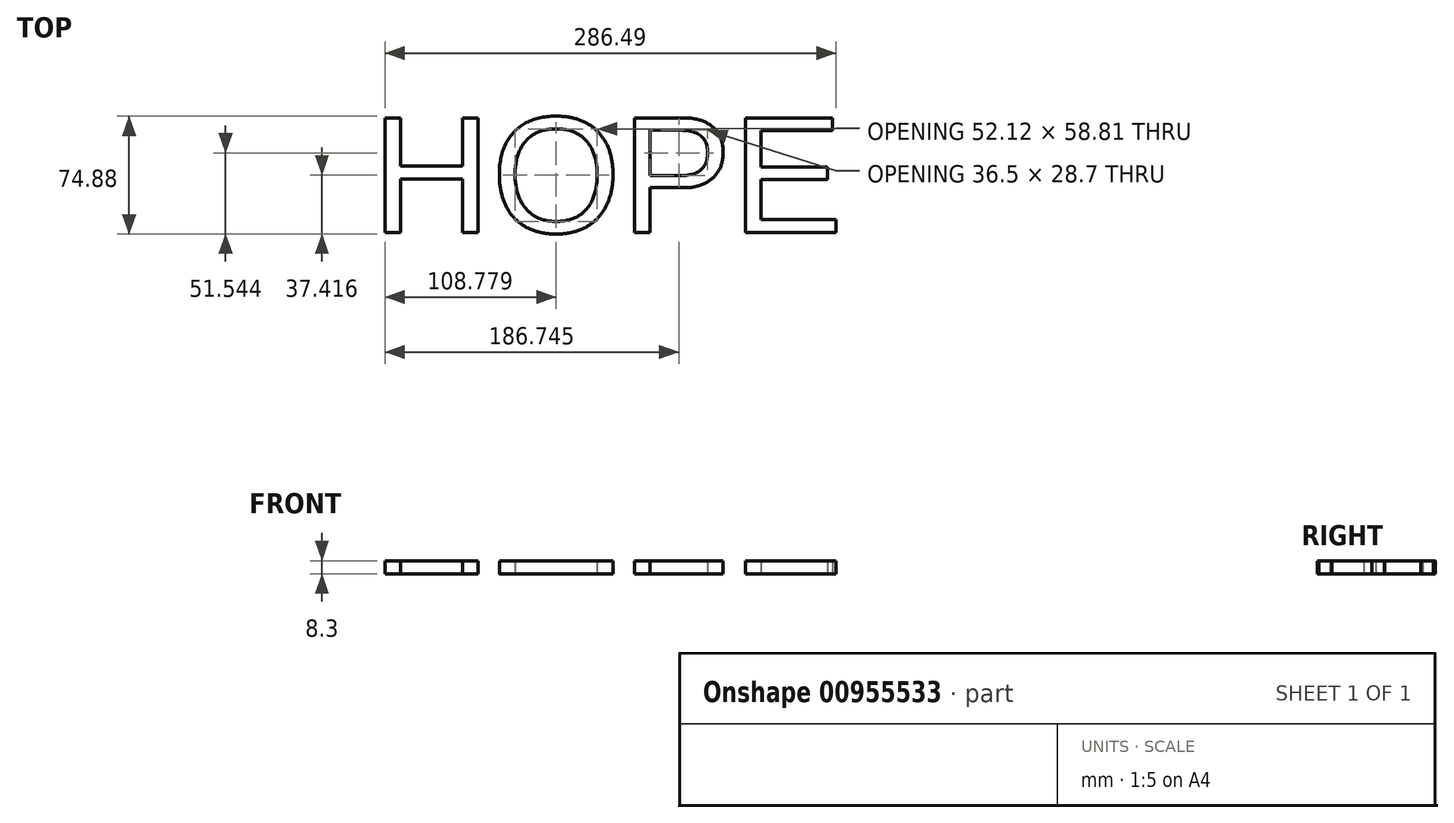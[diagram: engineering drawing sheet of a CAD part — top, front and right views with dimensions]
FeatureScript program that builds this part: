
annotation { "Feature Type Name" : "Feature", "Feature Type Description" : "" }
export const myFeature = defineFeature(function(context is Context, id is Id, definition is map)
    precondition{}
    {
        {
            var Q0;
            Q0=qCreatedBy(makeId("Top.planeOp"),FACE);
            var sketch = newSketch(context, id + "F0", { "sketchPlane" : qUnion([Q0])});
            skText(sketch, "E0", { "text": "HOPE", "fontName": "Arimo-Regular.ttf"});
            const initialGuessF0  = {"E0": [-0.07572, 0, 1, 0, 0.07614]};
            skSetInitialGuess(sketch, initialGuessF0);
            skSolve(sketch);
        }
        {
            var Q0;
            Q0 = qSketchRegion(id + "F0", true);
            extrude(context, id + "F1", {"entities" : qUnion([Q0]), "depth" : 8.3 * mm, "offsetDistance" : 25.4 * mm});
        }
    });
